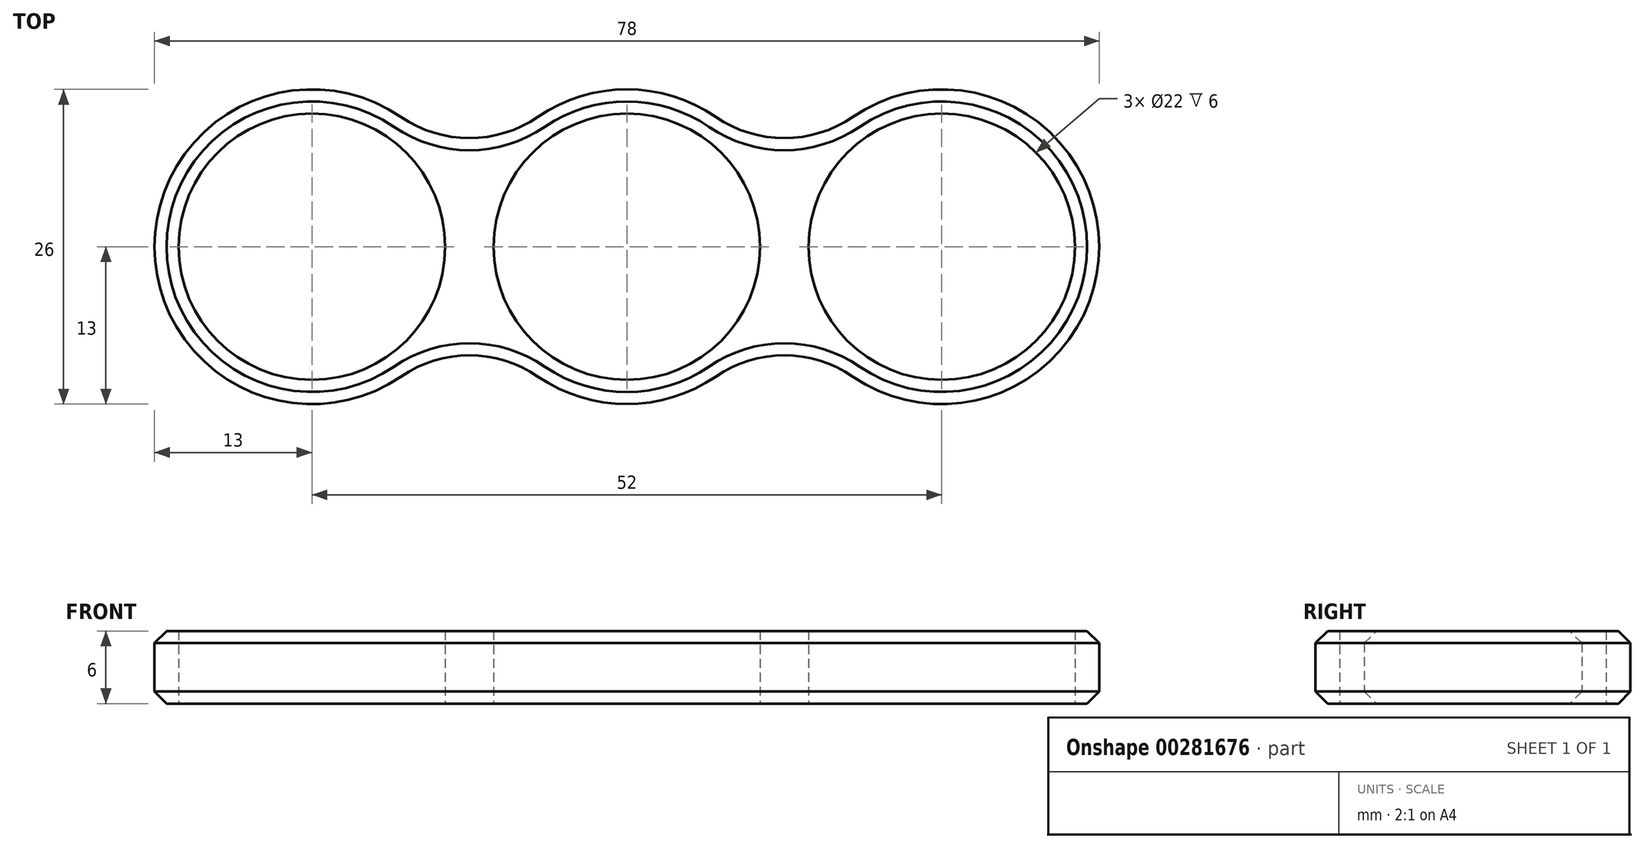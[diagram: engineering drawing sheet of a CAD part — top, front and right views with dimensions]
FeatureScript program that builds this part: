
annotation { "Feature Type Name" : "Feature", "Feature Type Description" : "" }
export const myFeature = defineFeature(function(context is Context, id is Id, definition is map)
    precondition{}
    {
        {
            var Q0;
            Q0=qCreatedBy(makeId("Top.planeOp"),FACE);
            var sketch = newSketch(context, id + "F0", { "sketchPlane" : qUnion([Q0])});
            skCircle(sketch, "E0", {"center": v(0, 0) * mm, "radius": 11 * mm});
            skCircle(sketch, "E1", {"center": v(26, 0) * mm, "radius": 11 * mm});
            skCircle(sketch, "E2", {"center": v(-26, 0) * mm, "radius": 11 * mm});
            skArc(sketch, "E3", {"start": v(-18.65, 10.72) * mm, "mid": v(-39, 0) * mm, "end": v(-18.65, -10.72) * mm});
            skArc(sketch, "E4", {"start": v(-7.35, -10.72) * mm, "mid": v(0, -13) * mm, "end": v(7.35, -10.72) * mm});
            skArc(sketch, "E5", {"start": v(18.65, -10.72) * mm, "mid": v(39, 0) * mm, "end": v(18.65, 10.72) * mm});
            skArc(sketch, "E6.trimOffspring", {"start": v(7.35, 10.72) * mm, "mid": v(0, 13) * mm, "end": v(-7.35, 10.72) * mm});
            skArc(sketch, "E7.filletArc", {"start": v(-18.65, 10.72) * mm, "mid": v(-13, 8.97) * mm, "end": v(-7.35, 10.72) * mm});
            skArc(sketch, "E8.filletArc", {"start": v(7.35, 10.72) * mm, "mid": v(13, 8.97) * mm, "end": v(18.65, 10.72) * mm});
            skArc(sketch, "E9.filletArc", {"start": v(18.65, -10.72) * mm, "mid": v(13, -8.97) * mm, "end": v(7.35, -10.72) * mm});
            skArc(sketch, "E10.filletArc", {"start": v(-7.35, -10.72) * mm, "mid": v(-13, -8.97) * mm, "end": v(-18.65, -10.72) * mm});
            skSolve(sketch);
        }
        {
            var Q0;
            Q0=makeQuery(id+"F0.imprint","IMPRINT",FACE,{"disambiguationData":[TD([[makeQuery(id+"F0.imprint","IMPRINT",EDGE,{"derivedFrom":sQuery(id+"F0.wireOp",EDGE,"E0")}),-1.0]])]});
            extrude(context, id + "F1", {"entities" : qUnion([Q0]), "depth" : 6 * mm});
        }
        {
            var Q0;
            Q0=makeQuery(id+"F1.opExtrude","CAP_EDGE",EDGE,{"disambiguationData":[OSD([sQuery(id+"F0.wireOp",EDGE,"E5")])],"isStart":false});
            var Q1;
            Q1=makeQuery(id+"F1.opExtrude","CAP_EDGE",EDGE,{"disambiguationData":[OSD([sQuery(id+"F0.wireOp",EDGE,"E5")])],"isStart":true});
            chamfer(context, id + "F2", {"entities" : qUnion([Q0, Q1]), "width" : 1 * mm, "tangentPropagation" : true});
        }
    });
